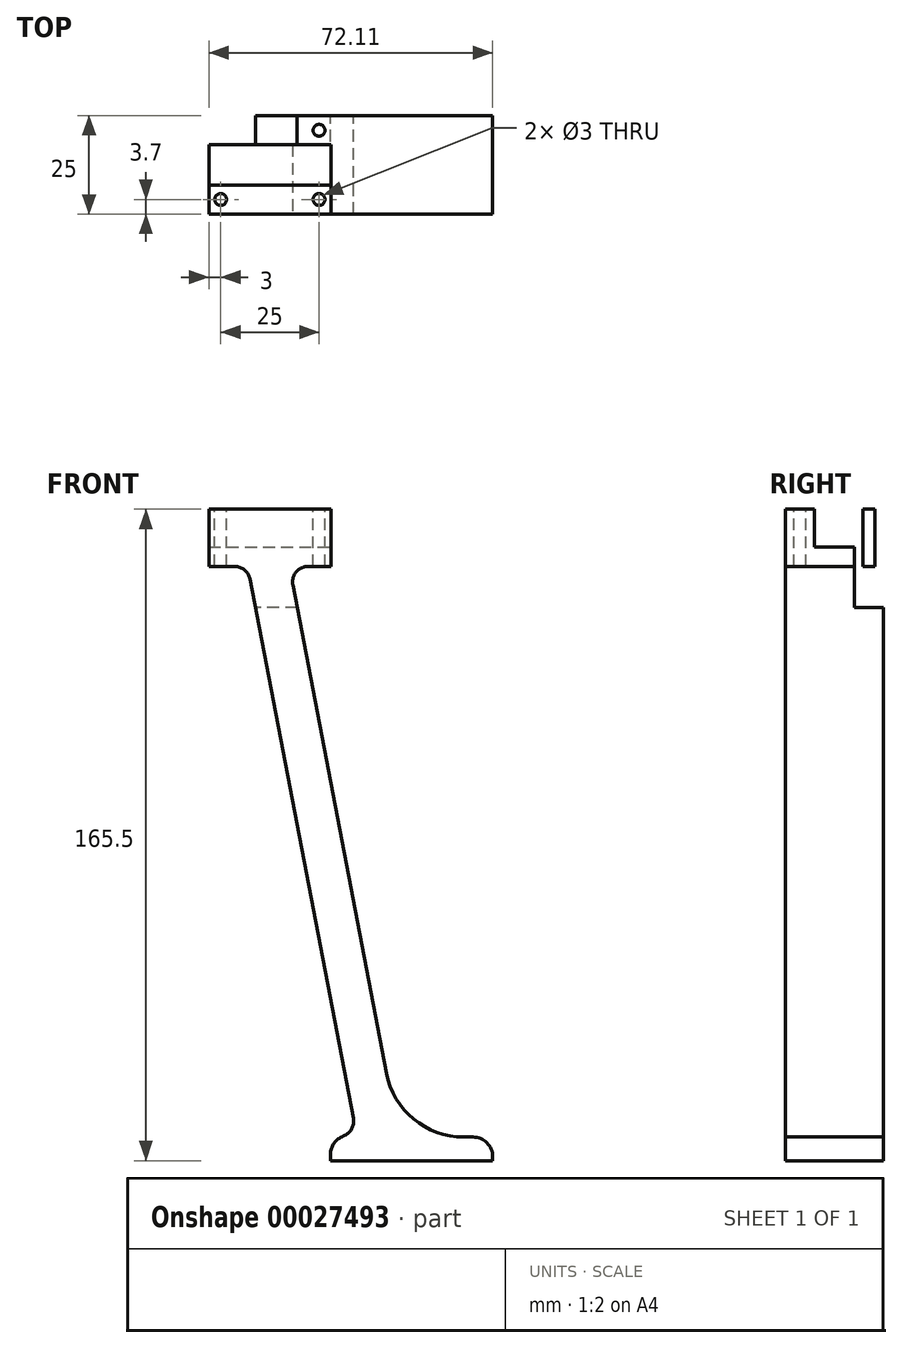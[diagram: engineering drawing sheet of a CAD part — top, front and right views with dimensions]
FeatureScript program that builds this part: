
annotation { "Feature Type Name" : "Feature", "Feature Type Description" : "" }
export const myFeature = defineFeature(function(context is Context, id is Id, definition is map)
    precondition{}
    {
        {
            var Q0;
            Q0=qCreatedBy(makeId("Front.planeOp"),FACE);
            var sketch = newSketch(context, id + "F0", { "sketchPlane" : qUnion([Q0])});
            skLineSegment(sketch, "E0.rect.bottom", {"start": v(12.5, -10) * mm, "end": v(1.92, -10) * mm});
            skLineSegment(sketch, "E0.rect.left", {"start": v(12.5, -10) * mm, "end": v(12.5, 4.5) * mm});
            skLineSegment(sketch, "E0.rect.right", {"start": v(-12.5, -10) * mm, "end": v(-12.5, 4.5) * mm});
            skPoint(sketch, "E0.rect.middle", {"position": v(0, 0) * mm});
            skLineSegment(sketch, "E1", {"start": v(-8.66, -10) * mm, "end": v(19.14, -155) * mm});
            skPoint(sketch, "E1.startSnap0", {"position": v(-12.5, 0) * mm});
            skLineSegment(sketch, "E2", {"start": v(1.92, -10) * mm, "end": v(29.71, -155) * mm});
            skPoint(sketch, "E3.orphan", {"position": v(-10.58, 0) * mm});
            skLineSegment(sketch, "E4.trimOffspring", {"start": v(-8.66, -10) * mm, "end": v(-12.5, -10) * mm});
            skLineSegment(sketch, "E5.bottom", {"start": v(12.4, -155) * mm, "end": v(19.14, -155) * mm});
            skLineSegment(sketch, "E5.top", {"start": v(12.4, -161) * mm, "end": v(53.6, -161) * mm});
            skLineSegment(sketch, "E5.left", {"start": v(12.4, -155) * mm, "end": v(12.4, -161) * mm});
            skLineSegment(sketch, "E5.right", {"start": v(53.6, -155) * mm, "end": v(53.6, -161) * mm});
            skLineSegment(sketch, "E6.trimOffspring", {"start": v(29.71, -155) * mm, "end": v(53.6, -155) * mm});
            skLineSegment(sketch, "E7", {"start": v(12.5, 4.5) * mm, "end": v(-12.5, 4.5) * mm});
            skPoint(sketch, "E8.orphan", {"position": v(12.5, 10) * mm});
            skPoint(sketch, "E9.orphan", {"position": v(-12.5, 10) * mm});
            skSolve(sketch);
        }
        {
            var Q0;
            Q0=makeQuery(id+"F0.imprint","IMPRINT",FACE,{"disambiguationData":[TD([[makeQuery(id+"F0.imprint","IMPRINT",EDGE,{"derivedFrom":sQuery(id+"F0.wireOp",EDGE,"E0.rect.bottom")}),-1.0]])]});
            var Q1;
            Q1=qSketchRegion(id+"F2",true);
            extrude(context, id + "F1", {"entities" : qUnion([Q0, Q1]), "depth" : 25 * mm});
        }
        {
            var Q0;
            Q0=makeQuery(id+"F1.opExtrude","SWEPT_FACE",FACE,{"disambiguationData":[OSD([sQuery(id+"F0.wireOp",EDGE,"E0.rect.left")])]});
            var sketch = newSketch(context, id + "F2", { "sketchPlane" : qUnion([Q0])});
            skPoint(sketch, "E10.centerSnap0", {"position": v(-12.5, -10) * mm});
            skLineSegment(sketch, "E11.rect.bottom", {"start": v(-7.4, -5.1) * mm, "end": v(-17.6, -5.1) * mm});
            skLineSegment(sketch, "E11.rect.top", {"start": v(-7.4, 5.1) * mm, "end": v(-17.6, 5.1) * mm});
            skLineSegment(sketch, "E11.rect.left", {"start": v(-7.4, -5.1) * mm, "end": v(-7.4, 5.1) * mm});
            skLineSegment(sketch, "E11.rect.right", {"start": v(-17.6, -5.1) * mm, "end": v(-17.6, 5.1) * mm});
            skPoint(sketch, "E11.rect.middle", {"position": v(-12.5, 0) * mm});
            skSolve(sketch);
        }
        {
            var Q0;
            Q0=makeQuery(id+"F2.imprint","IMPRINT",FACE,{"disambiguationData":[TD([[makeQuery(id+"F2.imprint","IMPRINT",EDGE,{"derivedFrom":sQuery(id+"F2.wireOp",EDGE,"E11.rect.bottom")}),-1.0]])]});
            extrude(context, id + "F3", {"entities" : qUnion([Q0]), "operationType" : NewBodyOperationType.REMOVE, "oppositeDirection" : true, "depth" : 25 * mm});
        }
        {
            var Q0;
            Q0=qSketchRegion(id+"F2",true);
            extrude(context, id + "F4", {"entities" : qUnion([Q0]), "operationType" : NewBodyOperationType.REMOVE, "oppositeDirection" : true, "depth" : 16 * mm});
        }
        {
            var Q0;
            Q0=makeQuery(id+"F1.opExtrude","SWEPT_FACE",FACE,{"disambiguationData":[OSD([sQuery(id+"F0.wireOp",EDGE,"E0.rect.right")])]});
            extrude(context, id + "F5", {"entities" : qUnion([Q0]), "operationType" : NewBodyOperationType.ADD, "depth" : 6 * mm});
        }
        {
            var Q0;
            {var subQ0=sQuery(id+"F0.wireOp",EDGE,"E7");var subQ1=sQuery(id+"F0.wireOp",EDGE,"E0.rect.right");var subQ5=makeQuery(id+"F3.opExtrude","SWEPT_FACE",FACE,{"disambiguationData":[OSD([sQuery(id+"F2.wireOp",EDGE,"E11.rect.left")])]});var subQ6=makeQuery(id+"F1.opExtrude","SWEPT_FACE",FACE,{"disambiguationData":[OSD([subQ0])]});Q0=makeQuery(id+"F5.boolean.opBoolean","MERGE",FACE,{"derivedFrom":[makeQuery(id+"F3.boolean.opBoolean","SPLIT",FACE,{"disambiguationData":[TD([subQ5])],"derivedFrom":subQ6}),makeQuery(id+"F5.opExtrude","SWEPT_FACE",FACE,{"disambiguationData":[OSD([subQ1,subQ0]),TDD([makeQuery(id+"F3.boolean.opBoolean","SPLIT",EDGE,{"disambiguationData":[TD([subQ5])],"derivedFrom":makeQuery(id+"F1.opExtrude","SWEPT_EDGE",EDGE,{"disambiguationData":[OSD([subQ1,subQ0])]})})])]})]});}
            var sketch = newSketch(context, id + "F6", { "sketchPlane" : qUnion([Q0])});
            skCircle(sketch, "E12", {"center": v(-15.5, -3.7) * mm, "radius": 1.5 * mm});
            skPoint(sketch, "E12.centerSnap0", {"position": v(-18.5, -3.7) * mm});
            skLineSegment(sketch, "E13", {"start": v(-3, 0) * mm, "end": v(-3, -7.4) * mm, "construction": true});
            skCircle(sketch, "E14.MirrorC", {"center": v(9.5, -3.7) * mm, "radius": 1.5 * mm});
            skSolve(sketch);
        }
        {
            var Q0;
            Q0=makeQuery(id+"F6.imprint","IMPRINT",FACE,{"disambiguationData":[TD([[makeQuery(id+"F6.imprint","IMPRINT",EDGE,{"derivedFrom":sQuery(id+"F6.wireOp",EDGE,"E12")}),1.0]])]});
            var Q1;
            Q1=makeQuery(id+"F6.imprint","IMPRINT",FACE,{"disambiguationData":[TD([[makeQuery(id+"F6.imprint","IMPRINT",EDGE,{"derivedFrom":sQuery(id+"F6.wireOp",EDGE,"E14.MirrorC")}),-1.0]])]});
            extrude(context, id + "F7", {"entities" : qUnion([Q0, Q1]), "operationType" : NewBodyOperationType.REMOVE, "oppositeDirection" : true, "depth" : 25 * mm});
        }
        {
            var Q0;
            {var subQ0=sQuery(id+"F0.wireOp",EDGE,"E7");var subQ1=sQuery(id+"F0.wireOp",EDGE,"E0.rect.right");var subQ5=makeQuery(id+"F3.opExtrude","SWEPT_FACE",FACE,{"disambiguationData":[OSD([sQuery(id+"F2.wireOp",EDGE,"E11.rect.right")])]});var subQ6=makeQuery(id+"F1.opExtrude","SWEPT_FACE",FACE,{"disambiguationData":[OSD([subQ0])]});Q0=makeQuery(id+"F5.boolean.opBoolean","MERGE",FACE,{"derivedFrom":[makeQuery(id+"F3.boolean.opBoolean","SPLIT",FACE,{"disambiguationData":[TD([subQ5])],"derivedFrom":subQ6}),makeQuery(id+"F5.opExtrude","SWEPT_FACE",FACE,{"disambiguationData":[OSD([subQ1,subQ0]),TDD([makeQuery(id+"F3.boolean.opBoolean","SPLIT",EDGE,{"disambiguationData":[TD([subQ5])],"derivedFrom":makeQuery(id+"F1.opExtrude","SWEPT_EDGE",EDGE,{"disambiguationData":[OSD([subQ1,subQ0])]})})])]})]});}
            var sketch = newSketch(context, id + "F8", { "sketchPlane" : qUnion([Q0])});
            skCircle(sketch, "E15", {"center": v(-15.5, -21.3) * mm, "radius": 1.5 * mm});
            skPoint(sketch, "E15.centerSnap0", {"position": v(-18.5, -21.3) * mm});
            skLineSegment(sketch, "E16", {"start": v(-3, -17.6) * mm, "end": v(-3, -25) * mm, "construction": true});
            skCircle(sketch, "E17.MirrorC", {"center": v(9.5, -21.3) * mm, "radius": 1.5 * mm});
            skSolve(sketch);
        }
        {
            var Q0;
            Q0=qSketchRegion(id+"F8",true);
            extrude(context, id + "F9", {"entities" : qUnion([Q0]), "operationType" : NewBodyOperationType.REMOVE, "oppositeDirection" : true, "depth" : 25 * mm});
        }
        {
            var Q0;
            Q0=makeQuery(id+"F1.opExtrude","SWEPT_EDGE",EDGE,{"disambiguationData":[OSD([sQuery(id+"F0.wireOp",EDGE,"E0.rect.bottom"),sQuery(id+"F0.wireOp",EDGE,"E2")])]});
            var Q1;
            Q1=makeQuery(id+"F1.opExtrude","SWEPT_EDGE",EDGE,{"disambiguationData":[OSD([sQuery(id+"F0.wireOp",EDGE,"E1"),sQuery(id+"F0.wireOp",EDGE,"E4.trimOffspring")])]});
            fillet(context, id + "F10", {"entities" : qUnion([Q0, Q1]), "radius" : 4 * mm, "tangentPropagation" : true, "allowEdgeOverflow" : false});
        }
        {
            var Q0;
            Q0=makeQuery(id+"F1.opExtrude","SWEPT_EDGE",EDGE,{"disambiguationData":[OSD([sQuery(id+"F0.wireOp",EDGE,"E2"),sQuery(id+"F0.wireOp",EDGE,"E6.trimOffspring")])]});
            fillet(context, id + "F11", {"entities" : qUnion([Q0]), "radius" : 20 * mm, "tangentPropagation" : true, "allowEdgeOverflow" : false});
        }
        {
            var Q0;
            Q0=makeQuery(id+"F1.opExtrude","SWEPT_EDGE",EDGE,{"disambiguationData":[OSD([sQuery(id+"F0.wireOp",EDGE,"E1"),sQuery(id+"F0.wireOp",EDGE,"E5.bottom")])]});
            fillet(context, id + "F12", {"entities" : qUnion([Q0]), "radius" : 4 * mm, "tangentPropagation" : true, "allowEdgeOverflow" : false});
        }
        {
            var Q0;
            Q0=makeQuery(id+"F1.opExtrude","SWEPT_EDGE",EDGE,{"disambiguationData":[OSD([sQuery(id+"F0.wireOp",EDGE,"E5.bottom"),sQuery(id+"F0.wireOp",EDGE,"E5.left")])]});
            var Q1;
            Q1=makeQuery(id+"F1.opExtrude","SWEPT_EDGE",EDGE,{"disambiguationData":[OSD([sQuery(id+"F0.wireOp",EDGE,"E5.right"),sQuery(id+"F0.wireOp",EDGE,"E6.trimOffspring")])]});
            fillet(context, id + "F13", {"entities" : qUnion([Q0, Q1]), "radius" : 5 * mm, "tangentPropagation" : true, "allowEdgeOverflow" : false});
        }
    });
